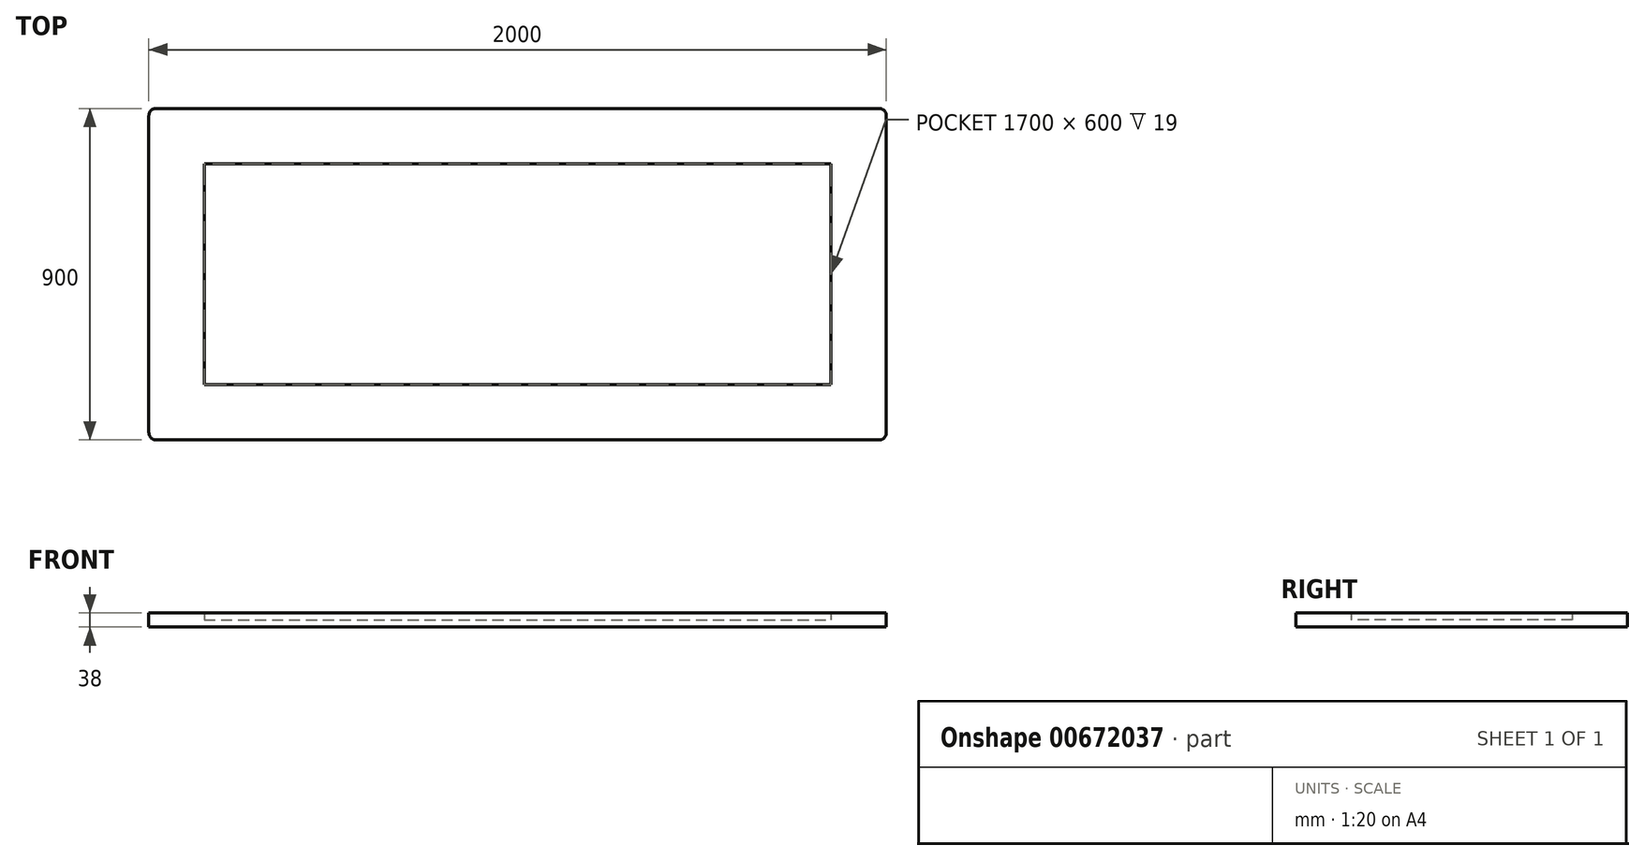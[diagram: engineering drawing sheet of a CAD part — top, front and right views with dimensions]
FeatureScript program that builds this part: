
annotation { "Feature Type Name" : "Feature", "Feature Type Description" : "" }
export const myFeature = defineFeature(function(context is Context, id is Id, definition is map)
    precondition{}
    {
        {
            var Q0;
            Q0=qCreatedBy(makeId("Top.planeOp"),FACE);
            var sketch = newSketch(context, id + "F0", { "sketchPlane" : qUnion([Q0])});
            skLineSegment(sketch, "E0.bottom", {"start": v(-996.05, 635.66) * mm, "end": v(1003.95, 635.66) * mm});
            skLineSegment(sketch, "E0.top", {"start": v(-996.05, -264.34) * mm, "end": v(1003.95, -264.34) * mm});
            skLineSegment(sketch, "E0.left", {"start": v(-996.05, 635.66) * mm, "end": v(-996.05, -264.34) * mm});
            skLineSegment(sketch, "E0.right", {"start": v(1003.95, 635.66) * mm, "end": v(1003.95, -264.34) * mm});
            skSolve(sketch);
        }
        {
            var Q0;
            Q0 = qSketchRegion(id + "F0", true);
            extrude(context, id + "F1", {"entities" : qUnion([Q0]), "depth" : 19 * mm, "offsetDistance" : 25 * mm});
        }
        {
            var Q0;
            Q0=makeQuery(id+"F1.opExtrude","CAP_FACE",FACE,{"disambiguationData":[OSD([sQuery(id+"F0.wireOp",EDGE,"E0.bottom"),sQuery(id+"F0.wireOp",EDGE,"E0.top"),sQuery(id+"F0.wireOp",EDGE,"E0.left"),sQuery(id+"F0.wireOp",EDGE,"E0.right")])],"isStart":false});
            var sketch = newSketch(context, id + "F2", { "sketchPlane" : qUnion([Q0])});
            skLineSegment(sketch, "E1.bottom", {"start": v(-996.05, 635.66) * mm, "end": v(1003.95, 635.66) * mm});
            skLineSegment(sketch, "E1.top", {"start": v(-996.05, -264.34) * mm, "end": v(1003.95, -264.34) * mm});
            skLineSegment(sketch, "E1.left", {"start": v(-996.05, 635.66) * mm, "end": v(-996.05, -264.34) * mm});
            skLineSegment(sketch, "E1.right", {"start": v(1003.95, 635.66) * mm, "end": v(1003.95, -264.34) * mm});
            skLineSegment(sketch, "E2.bottom", {"start": v(-846.05, 485.66) * mm, "end": v(853.95, 485.66) * mm});
            skLineSegment(sketch, "E2.top", {"start": v(-846.05, -114.34) * mm, "end": v(853.95, -114.34) * mm});
            skLineSegment(sketch, "E2.left", {"start": v(-846.05, 485.66) * mm, "end": v(-846.05, -114.34) * mm});
            skLineSegment(sketch, "E2.right", {"start": v(853.95, 485.66) * mm, "end": v(853.95, -114.34) * mm});
            skSolve(sketch);
        }
        {
            var Q0;
            Q0 = qSketchRegion(id + "F2", true);
            extrude(context, id + "F3", {"entities" : qUnion([Q0]), "operationType" : NewBodyOperationType.ADD, "depth" : 19 * mm, "offsetDistance" : 25 * mm});
        }
        {
            var Q0;
            Q0=makeQuery(id+"F3.boolean.opBoolean","MERGE",EDGE,{"derivedFrom":[makeQuery(id+"F1.opExtrude","SWEPT_EDGE",EDGE,{"disambiguationData":[OSD([sQuery(id+"F0.wireOp",EDGE,"E0.top"),sQuery(id+"F0.wireOp",EDGE,"E0.right")])]}),makeQuery(id+"F3.opExtrude","SWEPT_EDGE",EDGE,{"disambiguationData":[OSD([sQuery(id+"F2.wireOp",EDGE,"E1.top"),sQuery(id+"F2.wireOp",EDGE,"E1.right")])]})]});
            var Q1;
            Q1=makeQuery(id+"F3.boolean.opBoolean","MERGE",EDGE,{"derivedFrom":[makeQuery(id+"F1.opExtrude","SWEPT_EDGE",EDGE,{"disambiguationData":[OSD([sQuery(id+"F0.wireOp",EDGE,"E0.bottom"),sQuery(id+"F0.wireOp",EDGE,"E0.right")])]}),makeQuery(id+"F3.opExtrude","SWEPT_EDGE",EDGE,{"disambiguationData":[OSD([sQuery(id+"F2.wireOp",EDGE,"E1.bottom"),sQuery(id+"F2.wireOp",EDGE,"E1.right")])]})]});
            var Q2;
            Q2=makeQuery(id+"F3.boolean.opBoolean","MERGE",EDGE,{"derivedFrom":[makeQuery(id+"F1.opExtrude","SWEPT_EDGE",EDGE,{"disambiguationData":[OSD([sQuery(id+"F0.wireOp",EDGE,"E0.top"),sQuery(id+"F0.wireOp",EDGE,"E0.left")])]}),makeQuery(id+"F3.opExtrude","SWEPT_EDGE",EDGE,{"disambiguationData":[OSD([sQuery(id+"F2.wireOp",EDGE,"E1.top"),sQuery(id+"F2.wireOp",EDGE,"E1.left")])]})]});
            var Q3;
            Q3=makeQuery(id+"F3.boolean.opBoolean","MERGE",EDGE,{"derivedFrom":[makeQuery(id+"F1.opExtrude","SWEPT_EDGE",EDGE,{"disambiguationData":[OSD([sQuery(id+"F0.wireOp",EDGE,"E0.bottom"),sQuery(id+"F0.wireOp",EDGE,"E0.left")])]}),makeQuery(id+"F3.opExtrude","SWEPT_EDGE",EDGE,{"disambiguationData":[OSD([sQuery(id+"F2.wireOp",EDGE,"E1.bottom"),sQuery(id+"F2.wireOp",EDGE,"E1.left")])]})]});
            fillet(context, id + "F4", {"entities" : qUnion([Q0, Q1, Q2, Q3]), "radius" : 20 * mm, "tangentPropagation" : true, "allowEdgeOverflow" : false});
        }
    });
